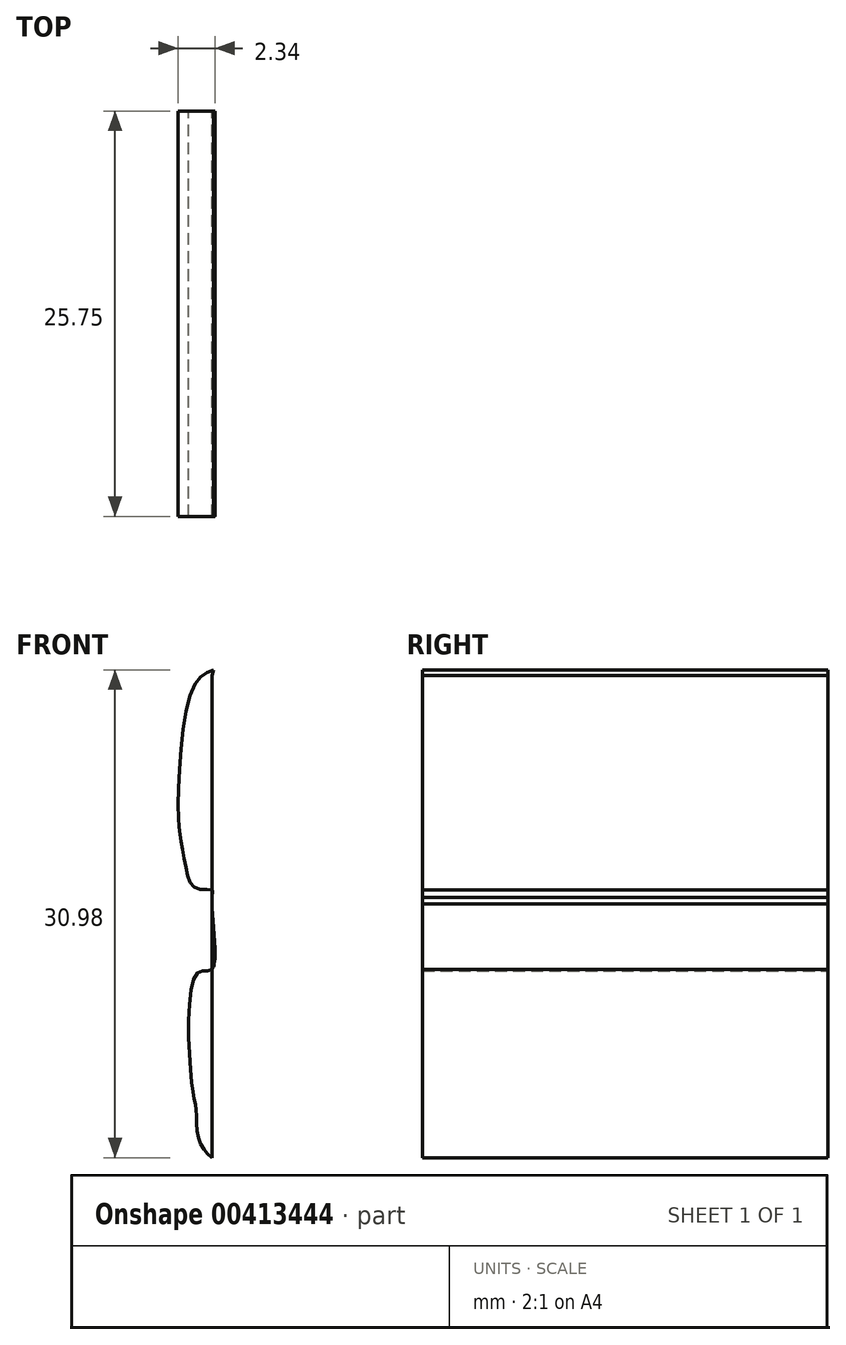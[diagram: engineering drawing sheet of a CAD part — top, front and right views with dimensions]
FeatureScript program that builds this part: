
annotation { "Feature Type Name" : "Feature", "Feature Type Description" : "" }
export const myFeature = defineFeature(function(context is Context, id is Id, definition is map)
    precondition{}
    {
        {
            var Q0;
            Q0=qCreatedBy(makeId("Front.planeOp"),FACE);
            var sketch = newSketch(context, id + "F0", { "sketchPlane" : qUnion([Q0])});
            skLineSegment(sketch, "E0", {"start": v(-84.82, 61.47) * mm, "end": v(-84.82, 30.85) * mm});
            skFitSpline(sketch, "E1", {"points": [v(-84.82, 30.85) * mm, v(-83.75, 24) * mm, v(-80.43, 20.35) * mm, v(-77.33, 19.82) * mm, v(-64.38, 18.96) * mm, v(-41.47, 18.32) * mm, v(-39, 18) * mm, v(-36.54, 16.93) * mm, v(-34.61, 15.1) * mm, v(-32.58, 11.47) * mm, v(-31.94, 8.26) * mm, v(-32.04, 1.94) * mm, v(-32.69, -5.55) * mm, v(-33.76, -10.05) * mm, v(-35.15, -14.33) * mm, v(-35.68, -15.62) * mm, v(-35.77, -16.83) * mm, v(-35.41, -17.58) * mm, v(-34.66, -18.27) * mm, v(-33.73, -18.51) * mm, v(-30.25, -18.63) * mm, v(-23.43, -18.9) * mm, v(-8.59, -19.54) * mm, v(8.75, -20.02) * mm, v(14.79, -20.17) * mm, v(16.26, -20.08) * mm, v(18.7, -19.69) * mm, v(22.39, -18.54) * mm, v(25.45, -16.98) * mm, v(27.58, -15.75) * mm, v(29.03, -15.2) * mm, v(30.38, -14.88) * mm, v(31.58, -14.79) * mm, v(32.93, -14.94) * mm, v(34.1, -15.2) * mm, v(35.34, -15.63) * mm, v(36.36, -16.23) * mm, v(37.29, -17.07) * mm, v(38.1, -17.97) * mm, v(38.28, -18.33) * mm, v(38.1, -18.63) * mm, v(38.76, -19.99) * mm, v(38.94, -20.08) * mm, v(39.18, -20.2) * mm, v(39.45, -20.77) * mm, v(39.36, -20.92) * mm, v(39.42, -21.04) * mm, v(39.18, -21.25) * mm, v(39.45, -22.12) * mm, v(39.63, -22.51) * mm, v(39.96, -22.63) * mm, v(40.32, -23.2) * mm, v(40.56, -23.3) * mm, v(40.44, -23.44) * mm, v(40.53, -23.65) * mm, v(40.3, -23.98) * mm, v(40.83, -25.24) * mm, v(41.1, -25.48) * mm, v(41.43, -25.78) * mm, v(41.64, -25.96) * mm, v(41.64, -26.12) * mm, v(41.52, -26.18) * mm, v(41.58, -26.48) * mm, v(41.43, -26.69) * mm, v(41.64, -27.44) * mm, v(41.88, -28.13) * mm, v(42.06, -28.13) * mm, v(42.19, -28.64) * mm, v(42.3, -29.63) * mm, v(42.28, -31.04) * mm, v(42.06, -32.87) * mm, v(41.73, -33.84) * mm, v(41.43, -34.92) * mm, v(41.28, -35.85) * mm, v(41.46, -36.84) * mm, v(42.03, -37.9) * mm, v(43.18, -38.91) * mm, v(44.35, -39.48) * mm, v(45.43, -39.96) * mm, v(46.33, -40.6) * mm, v(46.84, -41.14) * mm, v(47.05, -41.44) * mm, v(47.17, -41.59) * mm, v(47.17, -41.8) * mm, v(47.47, -42.4) * mm, v(47.6, -42.43) * mm, v(48.01, -43.12) * mm, v(48.2, -43.24) * mm, v(48.31, -43.39) * mm, v(48.2, -43.48) * mm, v(48.4, -44.26) * mm, v(48.61, -44.86) * mm, v(48.7, -45.13) * mm, v(48.88, -45.22) * mm, v(49.28, -46.1) * mm, v(49.28, -46.3) * mm, v(49.37, -46.7) * mm, v(49.4, -46.84) * mm, v(49.34, -46.96) * mm, v(49.49, -47.42) * mm, v(49.67, -47.42) * mm, v(50.09, -48.44) * mm, v(50.2, -48.62) * mm, v(50.36, -48.83) * mm, v(50.33, -49.04) * mm, v(50.33, -49.3) * mm, v(50.5, -49.97) * mm, v(50.6, -50.06) * mm, v(50.69, -50.39) * mm, v(50.78, -50.63) * mm, v(50.9, -50.93) * mm, v(50.96, -51.62) * mm, v(50.87, -52.91) * mm, v(50.75, -54.32) * mm, v(50.36, -55.62) * mm, v(49.97, -57.03) * mm, v(49.85, -58.14) * mm, v(49.97, -59.4) * mm, v(50.42, -60.42) * mm, v(51.08, -61.32) * mm, v(52.04, -62.32) * mm, v(53.45, -63.19) * mm, v(55.91, -64.09) * mm, v(57.78, -64.57) * mm, v(58.86, -64.45) * mm, v(59.49, -64.12) * mm, v(59.88, -63.49) * mm, v(60.1, -62.95) * mm, v(60.1, -61.99) * mm, v(60.03, -60.96) * mm, v(60.18, -60.48) * mm, v(60.48, -60) * mm, v(60.93, -59.73) * mm, v(61.6, -59.55) * mm, v(62.73, -59.61) * mm, v(64.2, -59.73) * mm, v(66.34, -59.8) * mm, v(71.69, -59.52) * mm, v(76.43, -58.98) * mm, v(80.49, -58.56) * mm, v(89, -57.69) * mm, v(108.55, -55.56) * mm, v(113.87, -54.9) * mm, v(113.9, -54.93) * mm, v(115.19, -56.82) * mm, v(115.82, -57.78) * mm, v(116.72, -58.41) * mm, v(116.84, -58.92) * mm, v(117.08, -59.07) * mm, v(117.56, -59.94) * mm, v(118.4, -60.48) * mm, v(119.18, -60.9) * mm, v(120.6, -61.05) * mm, v(121.77, -60.42) * mm, v(124.38, -57.96) * mm, v(125.22, -57) * mm, v(125.97, -55.62) * mm, v(126.6, -53.9) * mm, v(126.87, -51.2) * mm, v(126.72, -47.39) * mm, v(126.63, -45.01) * mm, v(126.24, -43.36) * mm, v(125.52, -41.56) * mm, v(125.73, -41.4) * mm, v(125.43, -40.33) * mm, v(124.98, -40.11) * mm, v(124.68, -38.97) * mm, v(124.65, -38.73) * mm, v(124.86, -38.55) * mm, v(124.3, -37.2) * mm, v(124.02, -37.17) * mm, v(123.87, -36.7) * mm, v(123.69, -36.5) * mm, v(123.5, -36.45) * mm, v(123.3, -36.03) * mm, v(123.5, -36) * mm, v(123.6, -35.9) * mm, v(123.15, -34.68) * mm, v(122.94, -34.53) * mm, v(122.7, -33.96) * mm, v(122.52, -33.78) * mm, v(122.04, -33.63) * mm, v(121.86, -33.27) * mm, v(122.19, -33) * mm, v(122.19, -32.81) * mm, v(121.7, -31.8) * mm, v(121.38, -31.67) * mm, v(121.14, -31.1) * mm, v(120.66, -30.92) * mm, v(120.42, -30.56) * mm, v(120.78, -30.41) * mm, v(120.2, -29.12) * mm, v(119.96, -29) * mm, v(119.72, -28.37) * mm, v(119.27, -28.28) * mm, v(118.91, -27.77) * mm, v(119.18, -27.62) * mm, v(118.61, -26.5) * mm, v(118.28, -26.33) * mm, v(118.07, -25.87) * mm, v(117.95, -25.72) * mm, v(117.38, -25.6) * mm, v(117.2, -25.33) * mm, v(117.41, -25.15) * mm, v(117.47, -25.1) * mm, v(117.44, -24.85) * mm, v(116.87, -23.86) * mm, v(116.63, -23.77) * mm, v(116.33, -23.17) * mm, v(115.73, -23.02) * mm, v(115.49, -22.72) * mm, v(115.3, -22.57) * mm, v(115.34, -21.88) * mm, v(114.86, -21.34) * mm, v(114.74, -21.19) * mm, v(114.74, -21.07) * mm, v(114.53, -20.77) * mm, v(114.35, -20.5) * mm, v(113.84, -20.44) * mm, v(113.75, -20.4) * mm, v(113.6, -20.26) * mm, v(113.36, -20.02) * mm, v(113.45, -19.75) * mm, v(113.42, -19.54) * mm, v(113.11, -19.27) * mm, v(112.9, -18.9) * mm, v(112.81, -18.75) * mm, v(112.7, -18.54) * mm, v(112.6, -18.4) * mm, v(112.33, -18.12) * mm, v(111.91, -17.97) * mm, v(111.64, -17.88) * mm, v(111.31, -17.5) * mm, v(111.28, -17.37) * mm, v(111.37, -17.31) * mm, v(111.4, -17.16) * mm, v(111.13, -16.65) * mm, v(110.9, -16.23) * mm, v(110.56, -15.84) * mm, v(110.38, -15.57) * mm, v(109.81, -15.51) * mm, v(109.5, -15.2) * mm, v(109.33, -14.94) * mm, v(109.6, -14.76) * mm, v(109.63, -14.55) * mm, v(109.5, -14.3) * mm, v(109.18, -13.83) * mm, v(109, -13.59) * mm, v(108.88, -13.5) * mm, v(108.7, -13.17) * mm, v(108.49, -13.02) * mm, v(108.22, -12.96) * mm, v(107.92, -12.93) * mm, v(107.56, -12.33) * mm, v(107.83, -11.94) * mm, v(107.74, -11.79) * mm, v(107.32, -11) * mm, v(107.2, -10.97) * mm, v(106.99, -10.58) * mm, v(106.72, -10.5) * mm, v(106.42, -10.4) * mm, v(106.05, -9.68) * mm, v(106.42, -9.35) * mm, v(106.36, -9.23) * mm, v(105.84, -8.36) * mm, v(105.7, -8.33) * mm, v(105.51, -7.9) * mm, v(104.97, -7.79) * mm, v(104.67, -7.13) * mm, v(104.7, -6.95) * mm, v(104.94, -6.62) * mm], "startDerivative": vector(23.82, -712.7) * mm, "endDerivative": vector(117.15, 149.33) * mm});
            skFitSpline(sketch, "E2", {"points": [v(104.94, -6.62) * mm, v(104.52, -5.63) * mm, v(104.28, -5.6) * mm, v(104.16, -5.18) * mm, v(103.68, -5.12) * mm, v(103.3, -4.15) * mm, v(103.62, -3.88) * mm, v(103.32, -2.95) * mm, v(103.17, -2.92) * mm, v(103.02, -2.44) * mm, v(102.9, -2.47) * mm, v(102.24, -0.6) * mm, v(101.49, 1.67) * mm, v(101.13, 2.97) * mm, v(100.2, 6.75) * mm, v(99.87, 8.94) * mm, v(99.69, 11.23) * mm, v(99.84, 13.42) * mm, v(100.1, 15.28) * mm, v(100.74, 17.12) * mm, v(101.52, 18.86) * mm, v(102.12, 19.97) * mm, v(103.35, 21.92) * mm, v(104.67, 23.54) * mm, v(106.54, 25.4) * mm, v(107.74, 26.16) * mm, v(109.2, 26.94) * mm, v(111.13, 27.7) * mm, v(113.23, 28.02) * mm, v(115.3, 28.14) * mm, v(115.52, 28.17) * mm, v(115.73, 28.02) * mm, v(115.9, 27.93) * mm, v(116.18, 28.11) * mm, v(116.48, 28.05) * mm, v(116.69, 28.41) * mm, v(116.87, 28.35) * mm, v(117.5, 28.62) * mm, v(118.67, 29.07) * mm, v(120, 29.97) * mm, v(121.38, 31.45) * mm, v(122.46, 33.67) * mm, v(122.6, 35.47) * mm, v(122.3, 37.33) * mm, v(121.83, 38.5) * mm, v(121.17, 39.4) * mm, v(120.75, 39.83) * mm, v(120.75, 40.79) * mm, v(120.63, 40.79) * mm, v(119.87, 40.76) * mm, v(119.57, 40.79) * mm, v(120.11, 41.03) * mm, v(120.72, 41.42) * mm, v(121.08, 41.84) * mm, v(121.05, 43.31) * mm, v(120.96, 44.36) * mm, v(121.23, 44.51) * mm, v(121.32, 44.87) * mm, v(120.66, 59.35) * mm, v(120.57, 63.44) * mm, v(120.11, 65.1) * mm, v(119.33, 66.32) * mm, v(118.2, 67.29) * mm, v(116.69, 67.77) * mm, v(112.54, 67.8) * mm, v(109, 67.83) * mm, v(108.79, 67.86) * mm, v(105.72, 71.64) * mm, v(105.3, 71.94) * mm, v(104.94, 72.18) * mm, v(104.16, 72.36) * mm, v(102.75, 72.54) * mm, v(100.83, 72.54) * mm, v(100.56, 72.36) * mm, v(98.18, 70.68) * mm, v(98.1, 70.44) * mm, v(97.52, 68.22) * mm, v(97.34, 68) * mm, v(97.1, 67.86) * mm, v(96.77, 67.86) * mm, v(69.7, 68.1) * mm, v(43.18, 68.22) * mm, v(20.31, 68.28) * mm, v(-12.97, 68.43) * mm, v(-43.47, 68.85) * mm, v(-67.77, 68.97) * mm, v(-67.89, 68.97) * mm, v(-69.06, 71.16) * mm, v(-69.27, 71.28) * mm, v(-73, 71.22) * mm, v(-73.27, 71.16) * mm, v(-74.68, 69.06) * mm, v(-74.77, 69.03) * mm, v(-76.81, 69) * mm, v(-77.65, 68.85) * mm, v(-80.57, 67.65) * mm, v(-82.04, 66.8) * mm, v(-83.45, 65.27) * mm, v(-84.23, 63.6) * mm, v(-84.53, 62.54) * mm, v(-84.82, 61.47) * mm], "startDerivative": vector(-45.96, 179.94) * mm, "endDerivative": vector(-38.32, -139.88) * mm});
            skFitSpline(sketch, "E3", {"points": [v(8.79, 15.58) * mm, v(-11.29, 17.56) * mm, v(-14.89, 16.4) * mm, v(-17.95, 14.68) * mm, v(-20.38, 11.89) * mm, v(-21.55, 9.73) * mm, v(-22.27, 5.86) * mm, v(-22.36, 1) * mm, v(-22, -2.42) * mm, v(-20.92, -5.13) * mm, v(-19.48, -7.47) * mm, v(-16.69, -9.72) * mm, v(-14.08, -10.8) * mm, v(-8.59, -11.43) * mm, v(1.77, -11.79) * mm, v(15.18, -11.97) * mm, v(19.41, -11.25) * mm, v(22.74, -9.18) * mm, v(25.44, -6.62) * mm, v(27.51, -2.24) * mm, v(28.05, 2.08) * mm, v(27.15, 6.49) * mm, v(26.16, 9.73) * mm, v(23.91, 12.43) * mm, v(21.12, 14.5) * mm, v(8.79, 15.58) * mm]});
            skFitSpline(sketch, "E4", {"points": [v(-84.72, 61.83) * mm, v(-86.01, 60.73) * mm, v(-86.96, 52.72) * mm, v(-86.77, 50.9) * mm, v(-86.4, 48.9) * mm, v(-85.82, 47.95) * mm, v(-84.82, 47.85) * mm, v(-84.82, 47.38) * mm, v(-84.82, 42.8) * mm, v(-85.72, 42.6) * mm, v(-86.1, 35.55) * mm, v(-85.82, 33.83) * mm, v(-85.63, 31.93) * mm, v(-84.82, 30.85) * mm], "startDerivative": vector(-20.78, -7.63) * mm, "endDerivative": vector(16.11, -15.14) * mm});
            skSolve(sketch);
        }
        {
            var Q0;
            {var subQ1=sQuery(id+"F0.wireOp",EDGE,"E1");Q0=makeQuery(id+"F0.imprint","IMPRINT",FACE,{"disambiguationData":[TD([[makeQuery(id+"F0.imprint","IMPRINT",EDGE,{"derivedFrom":subQ1}),1.0]])]});}
            var Q1;
            {var subQ0=sQuery(id+"F0.wireOp",EDGE,"E2");var subQ1=sQuery(id+"F0.wireOp",EDGE,"E0");var subQ2=makeQuery(id+"F0.imprint","INTERSECT",VERTEX,{"derivedFrom":[subQ1,subQ0]});Q1=makeQuery(id+"F0.imprint","IMPRINT",FACE,{"disambiguationData":[TD([[makeQuery(id+"F0.imprint","IMPRINT",EDGE,{"disambiguationData":[TD([[subQ2,-1.0]])],"derivedFrom":subQ1}),-1.0]])]});}
            var Q2;
            {var subQ0=sQuery(id+"F0.wireOp",EDGE,"E4");var subQ1=sQuery(id+"F0.wireOp",EDGE,"E0");var subQ3=makeQuery(id+"F0.imprint","INTERSECT",VERTEX,{"disambiguationData":[OD(3.0)],"derivedFrom":[subQ1,subQ0]});Q2=makeQuery(id+"F0.imprint","IMPRINT",FACE,{"disambiguationData":[TD([[makeQuery(id+"F0.imprint","IMPRINT",EDGE,{"disambiguationData":[TD([[subQ3,-1.0]])],"derivedFrom":subQ1}),-1.0]])]});}
            var Q3;
            {var subQ0=sQuery(id+"F0.wireOp",EDGE,"E4");var subQ1=sQuery(id+"F0.wireOp",EDGE,"E0");var subQ2=makeQuery(id+"F0.imprint","INTERSECT",VERTEX,{"disambiguationData":[OD(0.0)],"derivedFrom":[subQ1,subQ0]});Q3=makeQuery(id+"F0.imprint","IMPRINT",FACE,{"disambiguationData":[TD([[makeQuery(id+"F0.imprint","IMPRINT",EDGE,{"disambiguationData":[TD([[subQ2,-1.0]])],"derivedFrom":subQ1}),1.0]])]});}
            var Q4;
            {var subQ0=sQuery(id+"F0.wireOp",EDGE,"E4");var subQ1=sQuery(id+"F0.wireOp",EDGE,"E0");var subQ2=makeQuery(id+"F0.imprint","INTERSECT",VERTEX,{"disambiguationData":[OD(1.0)],"derivedFrom":[subQ1,subQ0]});Q4=makeQuery(id+"F0.imprint","IMPRINT",FACE,{"disambiguationData":[TD([[makeQuery(id+"F0.imprint","IMPRINT",EDGE,{"disambiguationData":[TD([[subQ2,-1.0]])],"derivedFrom":subQ1}),-1.0]])]});}
            var Q5;
            {var subQ0=sQuery(id+"F0.wireOp",EDGE,"E4");var subQ1=sQuery(id+"F0.wireOp",EDGE,"E0");var subQ2=makeQuery(id+"F0.imprint","INTERSECT",VERTEX,{"disambiguationData":[OD(2.0)],"derivedFrom":[subQ1,subQ0]});Q5=makeQuery(id+"F0.imprint","IMPRINT",FACE,{"disambiguationData":[TD([[makeQuery(id+"F0.imprint","IMPRINT",EDGE,{"disambiguationData":[TD([[subQ2,-1.0]])],"derivedFrom":subQ1}),1.0]])]});}
            extrude(context, id + "F1", {"entities" : qUnion([Q0, Q1, Q2, Q3, Q4, Q5]), "depth" : 25.75 * mm});
        }
    });
